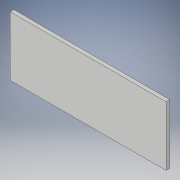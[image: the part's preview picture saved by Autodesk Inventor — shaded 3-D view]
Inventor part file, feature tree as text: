
AUTODESK INVENTOR PART (.ipt)
format: ipt  version: 2017 (Build 210142000, 142)  size: 86,016 bytes
history: native  units: in
note: dims shown in document units (in); Inventor stores cm internally (conversion verified against a paired STEP export)
features: extrude x1, sketch x1
ambient origin geometry x8: Origin, YZ Plane, XZ Plane, XY Plane, X Axis, Y Axis, Z Axis, Center Point
bodies: Solid1 (feature_tree)
feature tree (2):
  extrude  "Extrusion1"  Depth=2.0in
  sketch  "Sketch1"  dims[d0=5.25in d1=2.0in d2=0.125in d3=0.0in]
